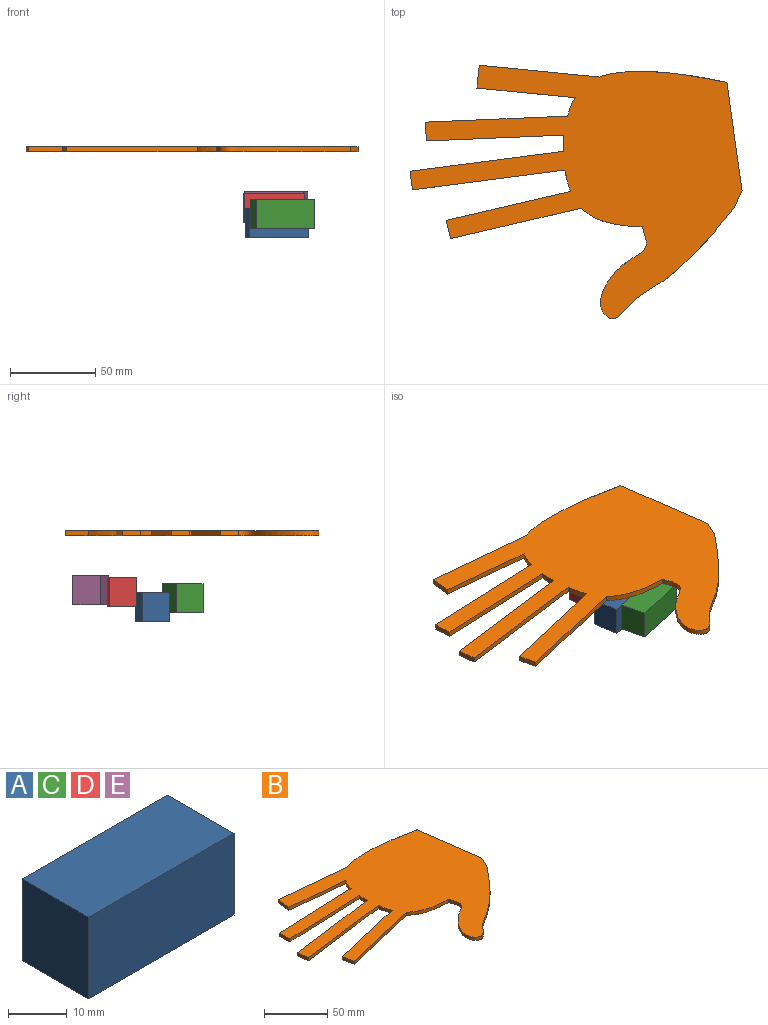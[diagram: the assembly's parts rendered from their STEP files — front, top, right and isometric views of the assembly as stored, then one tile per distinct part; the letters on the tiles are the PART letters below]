
ASSEMBLY  parts=5 mates=3
PART A: 6 faces, bbox 35x16x17 mm
  f0: plane 17x16mm, normal (1,0,0), area 272mm2, adj f1,f3,f4,f5
  f1: plane 35x17mm, normal (0,1,0), area 595mm2, adj f0,f2,f4,f5
  f2: plane 17x16mm, normal (-1,0,0), area 272mm2, adj f1,f3,f4,f5
  f3: plane 35x17mm, normal (0,-1,0), area 595mm2, adj f0,f2,f4,f5
  f4: plane 35x16mm, normal (0,0,1), area 560mm2, adj f0,f1,f2,f3
  f5: plane 35x16mm, normal (0,0,-1), area 560mm2, adj f0,f1,f2,f3
PART B: 22 faces, bbox 194.3x149.2x3 mm
  f0: plane 10.93x3mm, normal (-0.99,-0.13,0), area 33.1mm2, adj f1,f19,f20,f21
  f1: plane 89.29x11.58mm, normal (0.13,-0.99,0), area 270.1mm2, adj f0,f2,f20,f21
  f2: extruded ~12.46x3.19mm, area 38.7mm2, adj f1,f3,f20,f21
  f3: plane 72.67x16.94mm, normal (-0.23,0.97,0), area 223.9mm2, adj f2,f4,f20,f21
  f4: plane 10.74x3mm, normal (-0.97,-0.23,0), area 33.1mm2, adj f3,f5,f20,f21
  f5: plane 76.45x17.82mm, normal (0.23,-0.97,0), area 235.5mm2, adj f4,f6,f20,f21
  f6: extruded ~35.62x10.94mm, area 114.4mm2, adj f5,f7,f20,f21
  f7: extruded ~78.31x65.05mm, area 498.5mm2, adj f6,f8,f20,f21
  f8: plane 9.97x4.43mm, normal (0.91,-0.41,0), area 32.7mm2, adj f7,f9,f20,f21
  f9: plane 63.12x8.84mm, normal (0.99,0.14,0), area 191.2mm2, adj f8,f10,f20,f21
  f10: extruded ~74.6x6.65mm, area 227.7mm2, adj f9,f11,f20,f21
  f11: plane 70.36x6.94mm, normal (0.1,1,0), area 212.1mm2, adj f10,f12,f20,f21
  f12: plane 13.39x3mm, normal (-1,0.1,0), area 40.3mm2, adj f11,f13,f20,f21
  f13: plane 57.44x5.64mm, normal (-0.1,-1,0), area 173.1mm2, adj f12,f14,f20,f21
  f14: extruded ~10.77x4.52mm, area 35.1mm2, adj f13,f15,f20,f21
  f15: plane 83.04x3.52mm, normal (-0.04,1,0), area 249.3mm2, adj f14,f16,f20,f21
  f16: plane 11.01x3mm, normal (-1,-0.04,0), area 33.1mm2, adj f15,f17,f20,f21
  f17: plane 80.47x3.41mm, normal (0.04,-1,0), area 241.6mm2, adj f16,f18,f20,f21
  f18: extruded ~9.48x3mm, area 28.5mm2, adj f17,f19,f20,f21
  f19: plane 89.61x11.62mm, normal (-0.13,0.99,0), area 271.1mm2, adj f0,f18,f20,f21
  f20: plane 194.3x149.18mm, normal (0,0,1), area 13446mm2, adj f0,f1,f2,f3,f4,f5,f6,f7
  f21: plane 194.3x149.18mm, normal (0,0,-1), area 13446mm2, adj f0,f1,f2,f3,f4,f5,f6,f7
PART C: same geometry as A
PART D: same geometry as A
PART E: same geometry as A
PLACE A rot(axis=(0,0,1),7.4deg) t=(-11.65,-10.15,-45.97)mm
PLACE B t=(-18.39,-5.41,4.03)mm fixed
PLACE C rot(axis=(0,0,1),13.1deg) t=(-8.42,-27.91,-41)mm
PLACE D rot(axis=(0,0,1),2.4deg) t=(-13.38,7.75,-37.52)mm
PLACE E rot(axis=(0,0,-1),8.6deg) t=(-12.27,25.9,-36.31)mm
MATE parallel B.f5 <-> C.f3  axis (0.23,-0.97,0) through (-96.7,-51.62,5.53)mm
MATE parallel B.f1 <-> A.f3  axis (0.13,-0.99,0) through (-112.6,-26.18,5.53)mm
MATE parallel B.f17 <-> D.f3  axis (0.04,-1,0) through (-108.89,-1.65,5.53)mm
